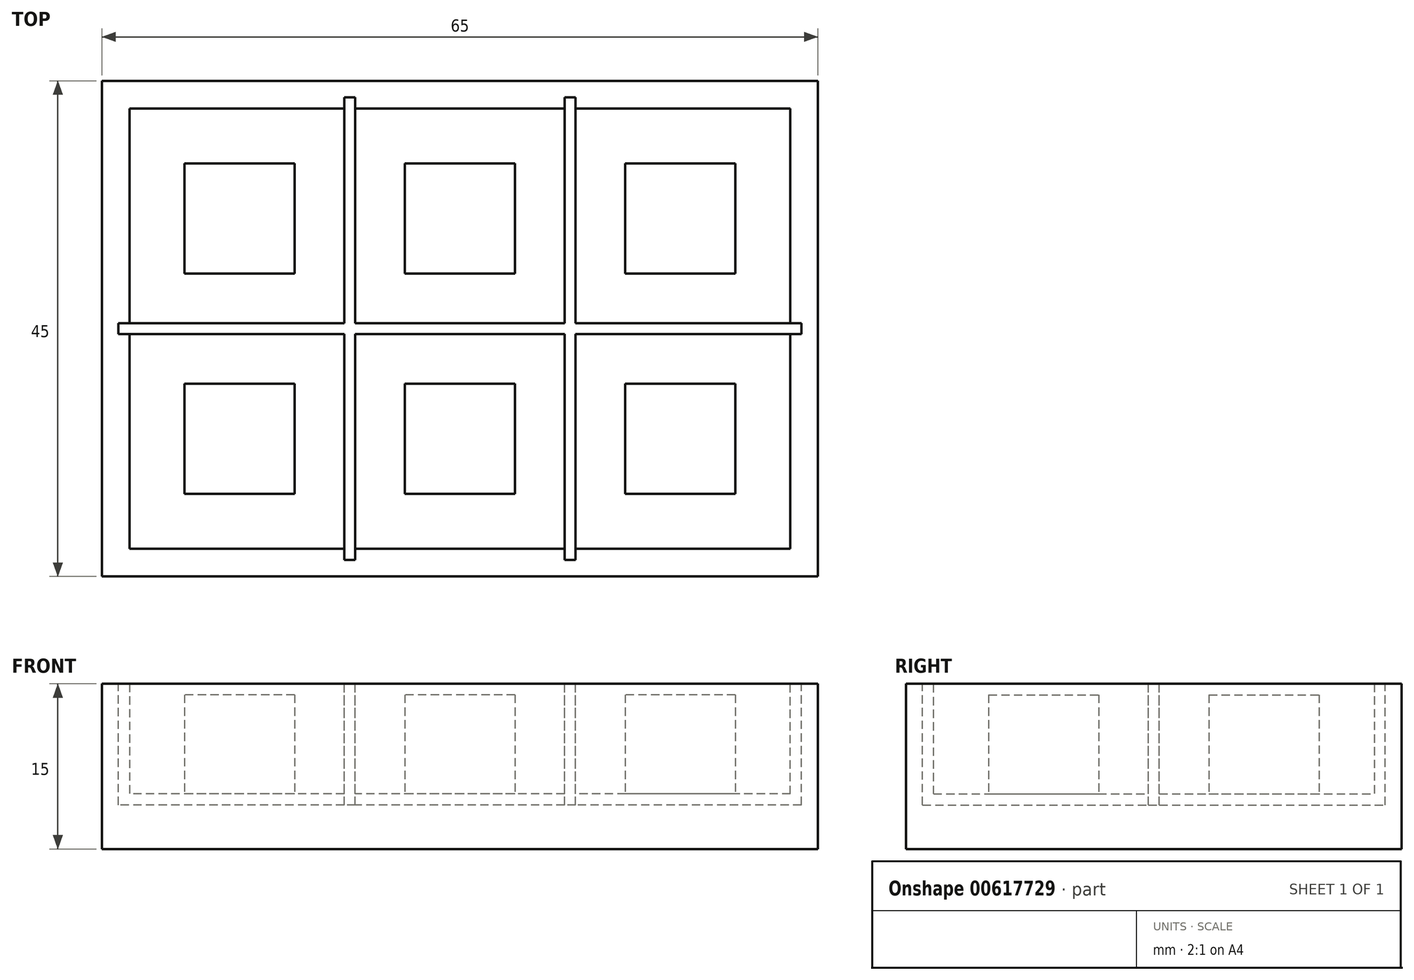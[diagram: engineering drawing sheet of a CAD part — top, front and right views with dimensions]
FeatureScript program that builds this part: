
annotation { "Feature Type Name" : "Feature", "Feature Type Description" : "" }
export const myFeature = defineFeature(function(context is Context, id is Id, definition is map)
    precondition{}
    {
        {
            var Q0;
            Q0=qCreatedBy(makeId("Top.planeOp"),FACE);
            var sketch = newSketch(context, id + "F0", { "sketchPlane" : qUnion([Q0])});
            skPoint(sketch, "E0.middle", {"position": v(0, 0) * mm});
            skLineSegment(sketch, "E1.bottom", {"start": v(32.5, -22.5) * mm, "end": v(-32.5, -22.5) * mm});
            skLineSegment(sketch, "E1.top", {"start": v(32.5, 22.5) * mm, "end": v(-32.5, 22.5) * mm});
            skLineSegment(sketch, "E1.left", {"start": v(32.5, -22.5) * mm, "end": v(32.5, 22.5) * mm});
            skLineSegment(sketch, "E1.right", {"start": v(-32.5, -22.5) * mm, "end": v(-32.5, 22.5) * mm});
            skSolve(sketch);
        }
        {
            var Q0;
            Q0=makeQuery(id+"F0.imprint","IMPRINT",FACE,{"disambiguationData":[TD([[makeQuery(id+"F0.imprint","IMPRINT",EDGE,{"derivedFrom":sQuery(id+"F0.wireOp",EDGE,"E1.bottom")}),-1.0]])]});
            extrude(context, id + "F1", {"entities" : qUnion([Q0]), "depth" : 5 * mm, "offsetDistance" : 25 * mm});
        }
        {
            var Q0;
            Q0=makeQuery(id+"F1.opExtrude","CAP_FACE",FACE,{"disambiguationData":[OSD([sQuery(id+"F0.wireOp",EDGE,"E1.bottom"),sQuery(id+"F0.wireOp",EDGE,"E1.top"),sQuery(id+"F0.wireOp",EDGE,"E1.left"),sQuery(id+"F0.wireOp",EDGE,"E1.right")])],"isStart":false});
            var sketch = newSketch(context, id + "F2", { "sketchPlane" : qUnion([Q0])});
            skLineSegment(sketch, "E2.bottom", {"start": v(32.5, -22.5) * mm, "end": v(-32.5, -22.5) * mm});
            skLineSegment(sketch, "E2.top", {"start": v(32.5, 22.5) * mm, "end": v(-32.5, 22.5) * mm});
            skLineSegment(sketch, "E2.left", {"start": v(32.5, -22.5) * mm, "end": v(32.5, 22.5) * mm});
            skLineSegment(sketch, "E2.right", {"start": v(-32.5, -22.5) * mm, "end": v(-32.5, 22.5) * mm});
            skPoint(sketch, "E2.middle", {"position": v(0, 0) * mm});
            skLineSegment(sketch, "E3.bottom", {"start": v(30, -20) * mm, "end": v(-30, -20) * mm});
            skLineSegment(sketch, "E3.top", {"start": v(30, 20) * mm, "end": v(-30, 20) * mm});
            skLineSegment(sketch, "E3.left", {"start": v(30, -20) * mm, "end": v(30, 20) * mm});
            skLineSegment(sketch, "E3.right", {"start": v(-30, -20) * mm, "end": v(-30, 20) * mm});
            skSolve(sketch);
        }
        {
            var Q0;
            Q0=makeQuery(id+"F2.imprint","IMPRINT",FACE,{"disambiguationData":[TD([[makeQuery(id+"F2.imprint","IMPRINT",EDGE,{"derivedFrom":sQuery(id+"F2.wireOp",EDGE,"E2.bottom")}),-1.0]])]});
            extrude(context, id + "F3", {"entities" : qUnion([Q0]), "operationType" : NewBodyOperationType.ADD, "depth" : 10 * mm, "offsetDistance" : 25 * mm});
        }
        {
            var Q0;
            Q0=makeQuery(id+"F1.opExtrude","CAP_FACE",FACE,{"disambiguationData":[OSD([sQuery(id+"F0.wireOp",EDGE,"E1.bottom"),sQuery(id+"F0.wireOp",EDGE,"E1.top"),sQuery(id+"F0.wireOp",EDGE,"E1.left"),sQuery(id+"F0.wireOp",EDGE,"E1.right")])],"isStart":false});
            var sketch = newSketch(context, id + "F4", { "sketchPlane" : qUnion([Q0])});
            skPoint(sketch, "E4.endSnap0", {"position": v(-5, 0) * mm});
            skLineSegment(sketch, "E5.bottom", {"start": v(-9.5, -21) * mm, "end": v(-10.5, -21) * mm});
            skLineSegment(sketch, "E5.top", {"start": v(-9.5, 21) * mm, "end": v(-10.5, 21) * mm});
            skLineSegment(sketch, "E5.left", {"start": v(-9.5, -21) * mm, "end": v(-9.5, 21) * mm});
            skLineSegment(sketch, "E5.right", {"start": v(-10.5, -21) * mm, "end": v(-10.5, 21) * mm});
            skPoint(sketch, "E5.middle", {"position": v(-10, 0) * mm});
            skLineSegment(sketch, "E6.bottom", {"start": v(10.5, -21) * mm, "end": v(9.5, -21) * mm});
            skLineSegment(sketch, "E6.top", {"start": v(10.5, 21) * mm, "end": v(9.5, 21) * mm});
            skLineSegment(sketch, "E6.left", {"start": v(10.5, -21) * mm, "end": v(10.5, 21) * mm});
            skLineSegment(sketch, "E6.right", {"start": v(9.5, -21) * mm, "end": v(9.5, 21) * mm});
            skPoint(sketch, "E6.middle", {"position": v(10, 0) * mm});
            skLineSegment(sketch, "E7.bottom", {"start": v(31, -0.5) * mm, "end": v(-31, -0.5) * mm});
            skLineSegment(sketch, "E7.top", {"start": v(31, 0.5) * mm, "end": v(-31, 0.5) * mm});
            skLineSegment(sketch, "E7.left", {"start": v(31, -0.5) * mm, "end": v(31, 0.5) * mm});
            skLineSegment(sketch, "E7.right", {"start": v(-31, -0.5) * mm, "end": v(-31, 0.5) * mm});
            skPoint(sketch, "E7.middle", {"position": v(0, 0) * mm});
            skSolve(sketch);
        }
        {
            var Q0;
            {var subQ0=sQuery(id+"F4.wireOp",EDGE,"E7.bottom");var subQ1=sQuery(id+"F4.wireOp",EDGE,"E5.right");var subQ2=makeQuery(id+"F4.imprint","INTERSECT",VERTEX,{"derivedFrom":[subQ1,subQ0]});Q0=makeQuery(id+"F4.imprint","IMPRINT",FACE,{"disambiguationData":[TD([[makeQuery(id+"F4.imprint","IMPRINT",EDGE,{"disambiguationData":[TD([[subQ2,-1.0]])],"derivedFrom":subQ1}),1.0]])]});}
            var Q1;
            {var subQ0=sQuery(id+"F4.wireOp",EDGE,"E7.bottom");var subQ1=sQuery(id+"F4.wireOp",EDGE,"E5.left");var subQ2=makeQuery(id+"F4.imprint","INTERSECT",VERTEX,{"derivedFrom":[subQ1,subQ0]});Q1=makeQuery(id+"F4.imprint","IMPRINT",FACE,{"disambiguationData":[TD([[makeQuery(id+"F4.imprint","IMPRINT",EDGE,{"disambiguationData":[TD([[subQ2,-1.0]])],"derivedFrom":subQ1}),1.0]])]});}
            var Q2;
            {var subQ0=sQuery(id+"F4.wireOp",EDGE,"E7.top");var subQ1=sQuery(id+"F4.wireOp",EDGE,"E5.left");var subQ2=makeQuery(id+"F4.imprint","INTERSECT",VERTEX,{"derivedFrom":[subQ1,subQ0]});Q2=makeQuery(id+"F4.imprint","IMPRINT",FACE,{"disambiguationData":[TD([[makeQuery(id+"F4.imprint","IMPRINT",EDGE,{"disambiguationData":[TD([[subQ2,-1.0]])],"derivedFrom":subQ1}),1.0]])]});}
            var Q3;
            {var subQ0=sQuery(id+"F4.wireOp",EDGE,"E7.bottom");var subQ1=sQuery(id+"F4.wireOp",EDGE,"E5.left");var subQ2=makeQuery(id+"F4.imprint","INTERSECT",VERTEX,{"derivedFrom":[subQ1,subQ0]});Q3=makeQuery(id+"F4.imprint","IMPRINT",FACE,{"disambiguationData":[TD([[makeQuery(id+"F4.imprint","IMPRINT",EDGE,{"disambiguationData":[TD([[subQ2,1.0]])],"derivedFrom":subQ1}),1.0]])]});}
            var Q4;
            {var subQ0=sQuery(id+"F4.wireOp",EDGE,"E7.bottom");var subQ1=sQuery(id+"F4.wireOp",EDGE,"E5.left");var subQ2=makeQuery(id+"F4.imprint","INTERSECT",VERTEX,{"derivedFrom":[subQ1,subQ0]});Q4=makeQuery(id+"F4.imprint","IMPRINT",FACE,{"disambiguationData":[TD([[makeQuery(id+"F4.imprint","IMPRINT",EDGE,{"disambiguationData":[TD([[subQ2,-1.0]])],"derivedFrom":subQ1}),-1.0]])]});}
            var Q5;
            {var subQ0=sQuery(id+"F4.wireOp",EDGE,"E7.top");var subQ1=sQuery(id+"F4.wireOp",EDGE,"E6.left");var subQ2=makeQuery(id+"F4.imprint","INTERSECT",VERTEX,{"derivedFrom":[subQ1,subQ0]});Q5=makeQuery(id+"F4.imprint","IMPRINT",FACE,{"disambiguationData":[TD([[makeQuery(id+"F4.imprint","IMPRINT",EDGE,{"disambiguationData":[TD([[subQ2,-1.0]])],"derivedFrom":subQ1}),1.0]])]});}
            var Q6;
            {var subQ0=sQuery(id+"F4.wireOp",EDGE,"E7.bottom");var subQ1=sQuery(id+"F4.wireOp",EDGE,"E6.left");var subQ2=makeQuery(id+"F4.imprint","INTERSECT",VERTEX,{"derivedFrom":[subQ1,subQ0]});Q6=makeQuery(id+"F4.imprint","IMPRINT",FACE,{"disambiguationData":[TD([[makeQuery(id+"F4.imprint","IMPRINT",EDGE,{"disambiguationData":[TD([[subQ2,1.0]])],"derivedFrom":subQ1}),1.0]])]});}
            var Q7;
            {var subQ0=sQuery(id+"F4.wireOp",EDGE,"E7.bottom");var subQ1=sQuery(id+"F4.wireOp",EDGE,"E6.left");var subQ2=makeQuery(id+"F4.imprint","INTERSECT",VERTEX,{"derivedFrom":[subQ1,subQ0]});Q7=makeQuery(id+"F4.imprint","IMPRINT",FACE,{"disambiguationData":[TD([[makeQuery(id+"F4.imprint","IMPRINT",EDGE,{"disambiguationData":[TD([[subQ2,-1.0]])],"derivedFrom":subQ1}),-1.0]])]});}
            var Q8;
            {var subQ0=sQuery(id+"F4.wireOp",EDGE,"E7.bottom");var subQ1=sQuery(id+"F4.wireOp",EDGE,"E6.left");var subQ2=makeQuery(id+"F4.imprint","INTERSECT",VERTEX,{"derivedFrom":[subQ1,subQ0]});Q8=makeQuery(id+"F4.imprint","IMPRINT",FACE,{"disambiguationData":[TD([[makeQuery(id+"F4.imprint","IMPRINT",EDGE,{"disambiguationData":[TD([[subQ2,-1.0]])],"derivedFrom":subQ1}),1.0]])]});}
            extrude(context, id + "F5", {"entities" : qUnion([Q0, Q1, Q2, Q3, Q4, Q5, Q6, Q7, Q8]), "operationType" : NewBodyOperationType.REMOVE, "oppositeDirection" : true, "depth" : 1 * mm, "offsetDistance" : 25 * mm});
        }
        {
            var Q0;
            {var subQ0=sQuery(id+"F2.wireOp",EDGE,"E3.top");var subQ1=makeQuery(id+"F3.opExtrude","CAP_EDGE",EDGE,{"disambiguationData":[OSD([subQ0])],"isStart":true});Q0=makeQuery(id+"F5.boolean.opBoolean","MERGE",FACE,{"derivedFrom":[makeQuery(id+"F3.opExtrude","SWEPT_FACE",FACE,{"disambiguationData":[OSD([subQ0])]}),makeQuery(id+"F5.opExtrude","SWEPT_FACE",FACE,{"disambiguationData":[OSD([subQ0]),TDD([makeQuery(id+"F4.imprint","IMPRINT",EDGE,{"disambiguationData":[TD([[makeQuery(id+"F4.imprint","INTERSECT",VERTEX,{"derivedFrom":[subQ1,sQuery(id+"F4.wireOp",EDGE,"E5.left")]}),-1.0]])],"derivedFrom":subQ1})])]}),makeQuery(id+"F5.opExtrude","SWEPT_FACE",FACE,{"disambiguationData":[OSD([subQ0]),TDD([makeQuery(id+"F4.imprint","IMPRINT",EDGE,{"disambiguationData":[TD([[makeQuery(id+"F4.imprint","INTERSECT",VERTEX,{"derivedFrom":[subQ1,sQuery(id+"F4.wireOp",EDGE,"E6.left")]}),-1.0]])],"derivedFrom":subQ1})])]})]});}
            var sketch = newSketch(context, id + "F6", { "sketchPlane" : qUnion([Q0])});
            skPoint(sketch, "E8.endSnap0", {"position": v(0, 5) * mm});
            skLineSegment(sketch, "E9.bottom", {"start": v(-10.5, 4) * mm, "end": v(-9.5, 4) * mm});
            skLineSegment(sketch, "E9.top", {"start": v(-10.5, 15) * mm, "end": v(-9.5, 15) * mm});
            skLineSegment(sketch, "E9.left", {"start": v(-10.5, 4) * mm, "end": v(-10.5, 15) * mm});
            skLineSegment(sketch, "E9.right", {"start": v(-9.5, 4) * mm, "end": v(-9.5, 15) * mm});
            skLineSegment(sketch, "E10.bottom", {"start": v(9.5, 4) * mm, "end": v(10.5, 4) * mm});
            skLineSegment(sketch, "E10.top", {"start": v(9.5, 15) * mm, "end": v(10.5, 15) * mm});
            skLineSegment(sketch, "E10.left", {"start": v(9.5, 4) * mm, "end": v(9.5, 15) * mm});
            skLineSegment(sketch, "E10.right", {"start": v(10.5, 4) * mm, "end": v(10.5, 15) * mm});
            skSolve(sketch);
        }
        {
            var Q0;
            {var subQ16=sQuery(id+"F6.wireOp",EDGE,"E9.bottom");Q0=makeQuery(id+"F6.imprint","IMPRINT",FACE,{"disambiguationData":[TD([[makeQuery(id+"F6.imprint","IMPRINT",EDGE,{"derivedFrom":subQ16}),-1.0]])]});}
            var Q1;
            {var subQ15=sQuery(id+"F6.wireOp",EDGE,"E10.bottom");Q1=makeQuery(id+"F6.imprint","IMPRINT",FACE,{"disambiguationData":[TD([[makeQuery(id+"F6.imprint","IMPRINT",EDGE,{"derivedFrom":subQ15}),-1.0]])]});}
            extrude(context, id + "F7", {"entities" : qUnion([Q0, Q1]), "operationType" : NewBodyOperationType.REMOVE, "oppositeDirection" : true, "depth" : 1 * mm, "offsetDistance" : 25 * mm});
        }
        {
            var Q0;
            {var subQ0=sQuery(id+"F2.wireOp",EDGE,"E3.left");Q0=makeQuery(id+"F5.boolean.opBoolean","MERGE",FACE,{"derivedFrom":[makeQuery(id+"F3.opExtrude","SWEPT_FACE",FACE,{"disambiguationData":[OSD([subQ0])]}),makeQuery(id+"F5.opExtrude","SWEPT_FACE",FACE,{"disambiguationData":[OSD([subQ0])]})]});}
            var sketch = newSketch(context, id + "F8", { "sketchPlane" : qUnion([Q0])});
            skLineSegment(sketch, "E11.bottom", {"start": v(-0.5, 4) * mm, "end": v(0.5, 4) * mm});
            skLineSegment(sketch, "E11.top", {"start": v(-0.5, 15) * mm, "end": v(0.5, 15) * mm});
            skLineSegment(sketch, "E11.left", {"start": v(-0.5, 4) * mm, "end": v(-0.5, 15) * mm});
            skLineSegment(sketch, "E11.right", {"start": v(0.5, 4) * mm, "end": v(0.5, 15) * mm});
            skSolve(sketch);
        }
        {
            var Q0;
            {var subQ0=sQuery(id+"F2.wireOp",EDGE,"E3.bottom");var subQ1=makeQuery(id+"F3.opExtrude","CAP_EDGE",EDGE,{"disambiguationData":[OSD([subQ0])],"isStart":true});Q0=makeQuery(id+"F5.boolean.opBoolean","MERGE",FACE,{"derivedFrom":[makeQuery(id+"F3.opExtrude","SWEPT_FACE",FACE,{"disambiguationData":[OSD([subQ0])]}),makeQuery(id+"F5.opExtrude","SWEPT_FACE",FACE,{"disambiguationData":[OSD([subQ0]),TDD([makeQuery(id+"F4.imprint","IMPRINT",EDGE,{"disambiguationData":[TD([[makeQuery(id+"F4.imprint","INTERSECT",VERTEX,{"derivedFrom":[subQ1,sQuery(id+"F4.wireOp",EDGE,"E5.left")]}),-1.0]])],"derivedFrom":subQ1})])]}),makeQuery(id+"F5.opExtrude","SWEPT_FACE",FACE,{"disambiguationData":[OSD([subQ0]),TDD([makeQuery(id+"F4.imprint","IMPRINT",EDGE,{"disambiguationData":[TD([[makeQuery(id+"F4.imprint","INTERSECT",VERTEX,{"derivedFrom":[subQ1,sQuery(id+"F4.wireOp",EDGE,"E6.left")]}),-1.0]])],"derivedFrom":subQ1})])]})]});}
            var sketch = newSketch(context, id + "F9", { "sketchPlane" : qUnion([Q0])});
            skLineSegment(sketch, "E12.bottom", {"start": v(-10.5, 4) * mm, "end": v(-9.5, 4) * mm});
            skLineSegment(sketch, "E12.top", {"start": v(-10.5, 15) * mm, "end": v(-9.5, 15) * mm});
            skLineSegment(sketch, "E12.left", {"start": v(-10.5, 4) * mm, "end": v(-10.5, 15) * mm});
            skLineSegment(sketch, "E12.right", {"start": v(-9.5, 4) * mm, "end": v(-9.5, 15) * mm});
            skLineSegment(sketch, "E13.bottom", {"start": v(9.5, 4) * mm, "end": v(10.5, 4) * mm});
            skLineSegment(sketch, "E13.top", {"start": v(9.5, 15) * mm, "end": v(10.5, 15) * mm});
            skLineSegment(sketch, "E13.left", {"start": v(9.5, 4) * mm, "end": v(9.5, 15) * mm});
            skLineSegment(sketch, "E13.right", {"start": v(10.5, 4) * mm, "end": v(10.5, 15) * mm});
            skSolve(sketch);
        }
        {
            var Q0;
            {var subQ0=sQuery(id+"F2.wireOp",EDGE,"E3.right");Q0=makeQuery(id+"F5.boolean.opBoolean","MERGE",FACE,{"derivedFrom":[makeQuery(id+"F3.opExtrude","SWEPT_FACE",FACE,{"disambiguationData":[OSD([subQ0])]}),makeQuery(id+"F5.opExtrude","SWEPT_FACE",FACE,{"disambiguationData":[OSD([subQ0])]})]});}
            var sketch = newSketch(context, id + "F10", { "sketchPlane" : qUnion([Q0])});
            skLineSegment(sketch, "E14.bottom", {"start": v(-0.5, 4) * mm, "end": v(0.5, 4) * mm});
            skLineSegment(sketch, "E14.top", {"start": v(-0.5, 15) * mm, "end": v(0.5, 15) * mm});
            skLineSegment(sketch, "E14.left", {"start": v(-0.5, 4) * mm, "end": v(-0.5, 15) * mm});
            skLineSegment(sketch, "E14.right", {"start": v(0.5, 4) * mm, "end": v(0.5, 15) * mm});
            skSolve(sketch);
        }
        {
            var Q0;
            {var subQ14=sQuery(id+"F10.wireOp",EDGE,"E14.bottom");Q0=makeQuery(id+"F10.imprint","IMPRINT",FACE,{"disambiguationData":[TD([[makeQuery(id+"F10.imprint","IMPRINT",EDGE,{"derivedFrom":subQ14}),1.0]])]});}
            extrude(context, id + "F11", {"entities" : qUnion([Q0]), "operationType" : NewBodyOperationType.REMOVE, "oppositeDirection" : true, "depth" : 1 * mm, "offsetDistance" : 25 * mm});
        }
        {
            var Q0;
            Q0 = qSketchRegion(id + "F9", true);
            extrude(context, id + "F12", {"entities" : qUnion([Q0]), "operationType" : NewBodyOperationType.REMOVE, "oppositeDirection" : true, "depth" : 1 * mm, "offsetDistance" : 25 * mm});
        }
        {
            var Q0;
            Q0 = qSketchRegion(id + "F8", true);
            extrude(context, id + "F13", {"entities" : qUnion([Q0]), "operationType" : NewBodyOperationType.REMOVE, "oppositeDirection" : true, "depth" : 1 * mm, "offsetDistance" : 25 * mm});
        }
        {
            var Q0;
            {var subQ0=sQuery(id+"F4.wireOp",EDGE,"E7.top");var subQ1=sQuery(id+"F4.wireOp",EDGE,"E5.left");var subQ2=makeQuery(id+"F4.imprint","INTERSECT",VERTEX,{"derivedFrom":[subQ1,subQ0]});Q0=makeQuery(id+"F5.boolean.opBoolean","SPLIT",FACE,{"disambiguationData":[TD([makeQuery(id+"F5.opExtrude","SWEPT_FACE",FACE,{"disambiguationData":[OSD([subQ1]),TDD([makeQuery(id+"F4.imprint","IMPRINT",EDGE,{"disambiguationData":[TD([[subQ2,-1.0]])],"derivedFrom":subQ1})])]})])],"derivedFrom":makeQuery(id+"F1.opExtrude","CAP_FACE",FACE,{"disambiguationData":[OSD([sQuery(id+"F0.wireOp",EDGE,"E1.bottom"),sQuery(id+"F0.wireOp",EDGE,"E1.top"),sQuery(id+"F0.wireOp",EDGE,"E1.left"),sQuery(id+"F0.wireOp",EDGE,"E1.right")])],"isStart":false})});}
            var sketch = newSketch(context, id + "F14", { "sketchPlane" : qUnion([Q0])});
            skLineSegment(sketch, "E15.bottom", {"start": v(5, 5) * mm, "end": v(-5, 5) * mm});
            skLineSegment(sketch, "E15.top", {"start": v(5, 15) * mm, "end": v(-5, 15) * mm});
            skLineSegment(sketch, "E15.left", {"start": v(5, 5) * mm, "end": v(5, 15) * mm});
            skLineSegment(sketch, "E15.right", {"start": v(-5, 5) * mm, "end": v(-5, 15) * mm});
            skPoint(sketch, "E15.middle", {"position": v(0, 10) * mm});
            skLineSegment(sketch, "E16.bottom", {"start": v(25, 5) * mm, "end": v(15, 5) * mm});
            skLineSegment(sketch, "E16.top", {"start": v(25, 15) * mm, "end": v(15, 15) * mm});
            skLineSegment(sketch, "E16.left", {"start": v(25, 5) * mm, "end": v(25, 15) * mm});
            skLineSegment(sketch, "E16.right", {"start": v(15, 5) * mm, "end": v(15, 15) * mm});
            skPoint(sketch, "E16.middle", {"position": v(20, 10) * mm});
            skLineSegment(sketch, "E17.bottom", {"start": v(25, -15) * mm, "end": v(15, -15) * mm});
            skLineSegment(sketch, "E17.top", {"start": v(25, -5) * mm, "end": v(15, -5) * mm});
            skLineSegment(sketch, "E17.left", {"start": v(25, -15) * mm, "end": v(25, -5) * mm});
            skLineSegment(sketch, "E17.right", {"start": v(15, -15) * mm, "end": v(15, -5) * mm});
            skPoint(sketch, "E17.middle", {"position": v(20, -10) * mm});
            skLineSegment(sketch, "E18.bottom", {"start": v(5, -15) * mm, "end": v(-5, -15) * mm});
            skLineSegment(sketch, "E18.top", {"start": v(5, -5) * mm, "end": v(-5, -5) * mm});
            skLineSegment(sketch, "E18.left", {"start": v(5, -15) * mm, "end": v(5, -5) * mm});
            skLineSegment(sketch, "E18.right", {"start": v(-5, -15) * mm, "end": v(-5, -5) * mm});
            skPoint(sketch, "E18.middle", {"position": v(0, -10) * mm});
            skLineSegment(sketch, "E19.bottom", {"start": v(-15, -15) * mm, "end": v(-25, -15) * mm});
            skLineSegment(sketch, "E19.top", {"start": v(-15, -5) * mm, "end": v(-25, -5) * mm});
            skLineSegment(sketch, "E19.left", {"start": v(-15, -15) * mm, "end": v(-15, -5) * mm});
            skLineSegment(sketch, "E19.right", {"start": v(-25, -15) * mm, "end": v(-25, -5) * mm});
            skPoint(sketch, "E19.middle", {"position": v(-20, -10) * mm});
            skLineSegment(sketch, "E20.bottom", {"start": v(-15, 5) * mm, "end": v(-25, 5) * mm});
            skLineSegment(sketch, "E20.top", {"start": v(-15, 15) * mm, "end": v(-25, 15) * mm});
            skLineSegment(sketch, "E20.left", {"start": v(-15, 5) * mm, "end": v(-15, 15) * mm});
            skLineSegment(sketch, "E20.right", {"start": v(-25, 5) * mm, "end": v(-25, 15) * mm});
            skPoint(sketch, "E20.middle", {"position": v(-20, 10) * mm});
            skSolve(sketch);
        }
        {
            var Q0;
            Q0=makeQuery(id+"F14.imprint","IMPRINT",FACE,{"disambiguationData":[TD([[makeQuery(id+"F14.imprint","IMPRINT",EDGE,{"derivedFrom":sQuery(id+"F14.wireOp",EDGE,"E20.bottom")}),-1.0]])]});
            var Q1;
            Q1=makeQuery(id+"F14.imprint","IMPRINT",FACE,{"disambiguationData":[TD([[makeQuery(id+"F14.imprint","IMPRINT",EDGE,{"derivedFrom":sQuery(id+"F14.wireOp",EDGE,"E15.bottom")}),-1.0]])]});
            var Q2;
            Q2=makeQuery(id+"F14.imprint","IMPRINT",FACE,{"disambiguationData":[TD([[makeQuery(id+"F14.imprint","IMPRINT",EDGE,{"derivedFrom":sQuery(id+"F14.wireOp",EDGE,"E16.bottom")}),-1.0]])]});
            var Q3;
            Q3=makeQuery(id+"F14.imprint","IMPRINT",FACE,{"disambiguationData":[TD([[makeQuery(id+"F14.imprint","IMPRINT",EDGE,{"derivedFrom":sQuery(id+"F14.wireOp",EDGE,"E17.bottom")}),-1.0]])]});
            var Q4;
            Q4=makeQuery(id+"F14.imprint","IMPRINT",FACE,{"disambiguationData":[TD([[makeQuery(id+"F14.imprint","IMPRINT",EDGE,{"derivedFrom":sQuery(id+"F14.wireOp",EDGE,"E18.bottom")}),-1.0]])]});
            var Q5;
            Q5=makeQuery(id+"F14.imprint","IMPRINT",FACE,{"disambiguationData":[TD([[makeQuery(id+"F14.imprint","IMPRINT",EDGE,{"derivedFrom":sQuery(id+"F14.wireOp",EDGE,"E19.bottom")}),-1.0]])]});
            extrude(context, id + "F15", {"entities" : qUnion([Q0, Q1, Q2, Q3, Q4, Q5]), "operationType" : NewBodyOperationType.ADD, "depth" : 9 * mm, "offsetDistance" : 25 * mm});
        }
    });
